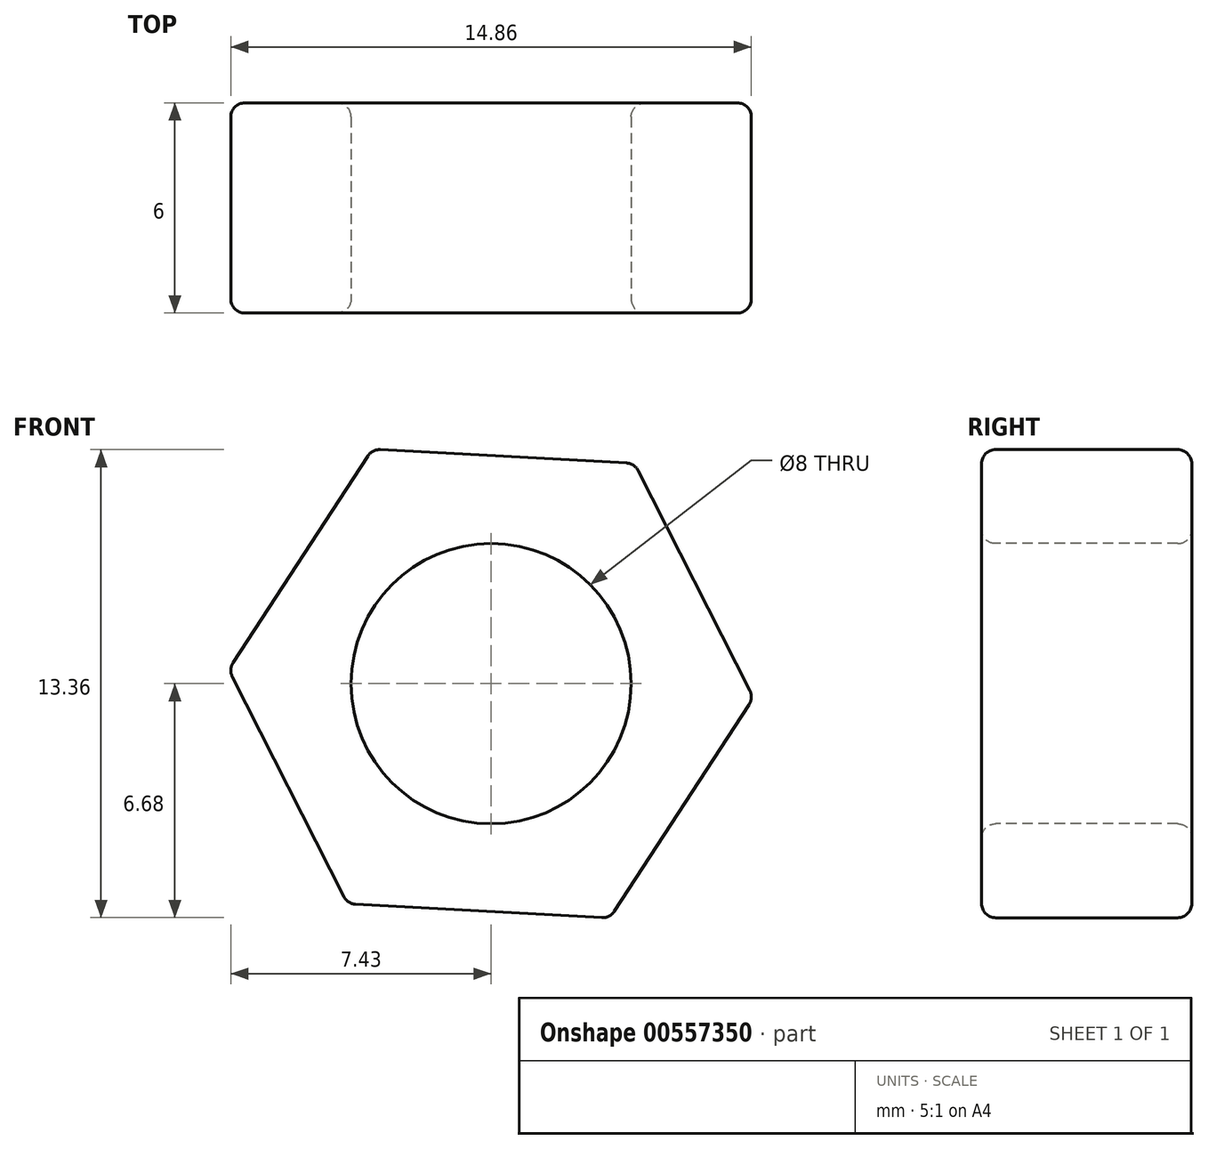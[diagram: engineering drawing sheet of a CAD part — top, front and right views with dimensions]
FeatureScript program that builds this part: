
annotation { "Feature Type Name" : "Feature", "Feature Type Description" : "" }
export const myFeature = defineFeature(function(context is Context, id is Id, definition is map)
    precondition{}
    {
        {
            var Q0;
            Q0=qCreatedBy(makeId("Front.planeOp"),FACE);
            var sketch = newSketch(context, id + "F0", { "sketchPlane" : qUnion([Q0])});
            skCircle(sketch, "E0.cCircle", {"center": v(0, 0) * mm, "radius": 6.5 * mm, "construction": true});
            skLineSegment(sketch, "E0.0", {"start": v(7.5, -0.4) * mm, "end": v(3.4, -6.7) * mm});
            skLineSegment(sketch, "E0.1", {"start": v(3.4, -6.7) * mm, "end": v(-4.1, -6.29) * mm});
            skLineSegment(sketch, "E0.2", {"start": v(-4.1, -6.29) * mm, "end": v(-7.5, 0.4) * mm});
            skLineSegment(sketch, "E0.3", {"start": v(-7.5, 0.4) * mm, "end": v(-3.4, 6.7) * mm});
            skLineSegment(sketch, "E0.4", {"start": v(-3.4, 6.7) * mm, "end": v(4.1, 6.29) * mm});
            skLineSegment(sketch, "E0.5", {"start": v(4.1, 6.29) * mm, "end": v(7.5, -0.4) * mm});
            skPoint(sketch, "E0.0.midPoint", {"position": v(5.44, -3.55) * mm});
            skSolve(sketch);
        }
        {
            var Q0;
            Q0=qSketchRegion(id+"F0",true);
            extrude(context, id + "F1", {"entities" : qUnion([Q0]), "depth" : 6 * mm, "offsetDistance" : 25 * mm});
        }
        {
            var Q0;
            Q0=makeQuery(id+"F1.opExtrude","CAP_FACE",FACE,{"disambiguationData":[OSD([sQuery(id+"F0.wireOp",EDGE,"E0.0"),sQuery(id+"F0.wireOp",EDGE,"E0.1"),sQuery(id+"F0.wireOp",EDGE,"E0.2"),sQuery(id+"F0.wireOp",EDGE,"E0.3"),sQuery(id+"F0.wireOp",EDGE,"E0.4"),sQuery(id+"F0.wireOp",EDGE,"E0.5")])],"isStart":false});
            var sketch = newSketch(context, id + "F2", { "sketchPlane" : qUnion([Q0])});
            skCircle(sketch, "E1", {"center": v(0, 0) * mm, "radius": 4 * mm});
            skSolve(sketch);
        }
        {
            var Q0;
            Q0=makeQuery(id+"F2.imprint","IMPRINT",FACE,{"disambiguationData":[TD([[makeQuery(id+"F2.imprint","IMPRINT",EDGE,{"derivedFrom":sQuery(id+"F2.wireOp",EDGE,"E1")}),-1.0]])]});
            extrude(context, id + "F3", {"entities" : qUnion([Q0]), "operationType" : NewBodyOperationType.INTERSECT, "oppositeDirection" : true, "depth" : 6 * mm, "offsetDistance" : 25 * mm});
        }
        {
            var Q0;
            Q0=makeQuery(id+"F1.opExtrude","SWEPT_EDGE",EDGE,{"disambiguationData":[OSD([sQuery(id+"F0.wireOp",EDGE,"E0.2"),sQuery(id+"F0.wireOp",EDGE,"E0.3")])]});
            var Q1;
            Q1=makeQuery(id+"F1.opExtrude","SWEPT_FACE",FACE,{"disambiguationData":[OSD([sQuery(id+"F0.wireOp",EDGE,"E0.2")])]});
            var Q2;
            Q2=makeQuery(id+"F1.opExtrude","SWEPT_FACE",FACE,{"disambiguationData":[OSD([sQuery(id+"F0.wireOp",EDGE,"E0.1")])]});
            var Q3;
            Q3=makeQuery(id+"F1.opExtrude","SWEPT_FACE",FACE,{"disambiguationData":[OSD([sQuery(id+"F0.wireOp",EDGE,"E0.3")])]});
            var Q4;
            Q4=makeQuery(id+"F1.opExtrude","SWEPT_FACE",FACE,{"disambiguationData":[OSD([sQuery(id+"F0.wireOp",EDGE,"E0.4")])]});
            var Q5;
            Q5=makeQuery(id+"F1.opExtrude","SWEPT_FACE",FACE,{"disambiguationData":[OSD([sQuery(id+"F0.wireOp",EDGE,"E0.5")])]});
            var Q6;
            Q6=makeQuery(id+"F1.opExtrude","SWEPT_FACE",FACE,{"disambiguationData":[OSD([sQuery(id+"F0.wireOp",EDGE,"E0.0")])]});
            var Q7;
            Q7=makeQuery(id+"F1.opExtrude","CAP_FACE",FACE,{"disambiguationData":[OSD([sQuery(id+"F0.wireOp",EDGE,"E0.0"),sQuery(id+"F0.wireOp",EDGE,"E0.1"),sQuery(id+"F0.wireOp",EDGE,"E0.2"),sQuery(id+"F0.wireOp",EDGE,"E0.3"),sQuery(id+"F0.wireOp",EDGE,"E0.4"),sQuery(id+"F0.wireOp",EDGE,"E0.5")])],"isStart":false});
            var Q8;
            Q8=makeQuery(id+"F1.opExtrude","CAP_FACE",FACE,{"disambiguationData":[OSD([sQuery(id+"F0.wireOp",EDGE,"E0.0"),sQuery(id+"F0.wireOp",EDGE,"E0.1"),sQuery(id+"F0.wireOp",EDGE,"E0.2"),sQuery(id+"F0.wireOp",EDGE,"E0.3"),sQuery(id+"F0.wireOp",EDGE,"E0.4"),sQuery(id+"F0.wireOp",EDGE,"E0.5")])],"isStart":true});
            fillet(context, id + "F4", {"entities" : qUnion([Q0, Q1, Q2, Q3, Q4, Q5, Q6, Q7, Q8]), "radius" : 0.4 * mm, "tangentPropagation" : true, "allowEdgeOverflow" : false});
        }
    });
